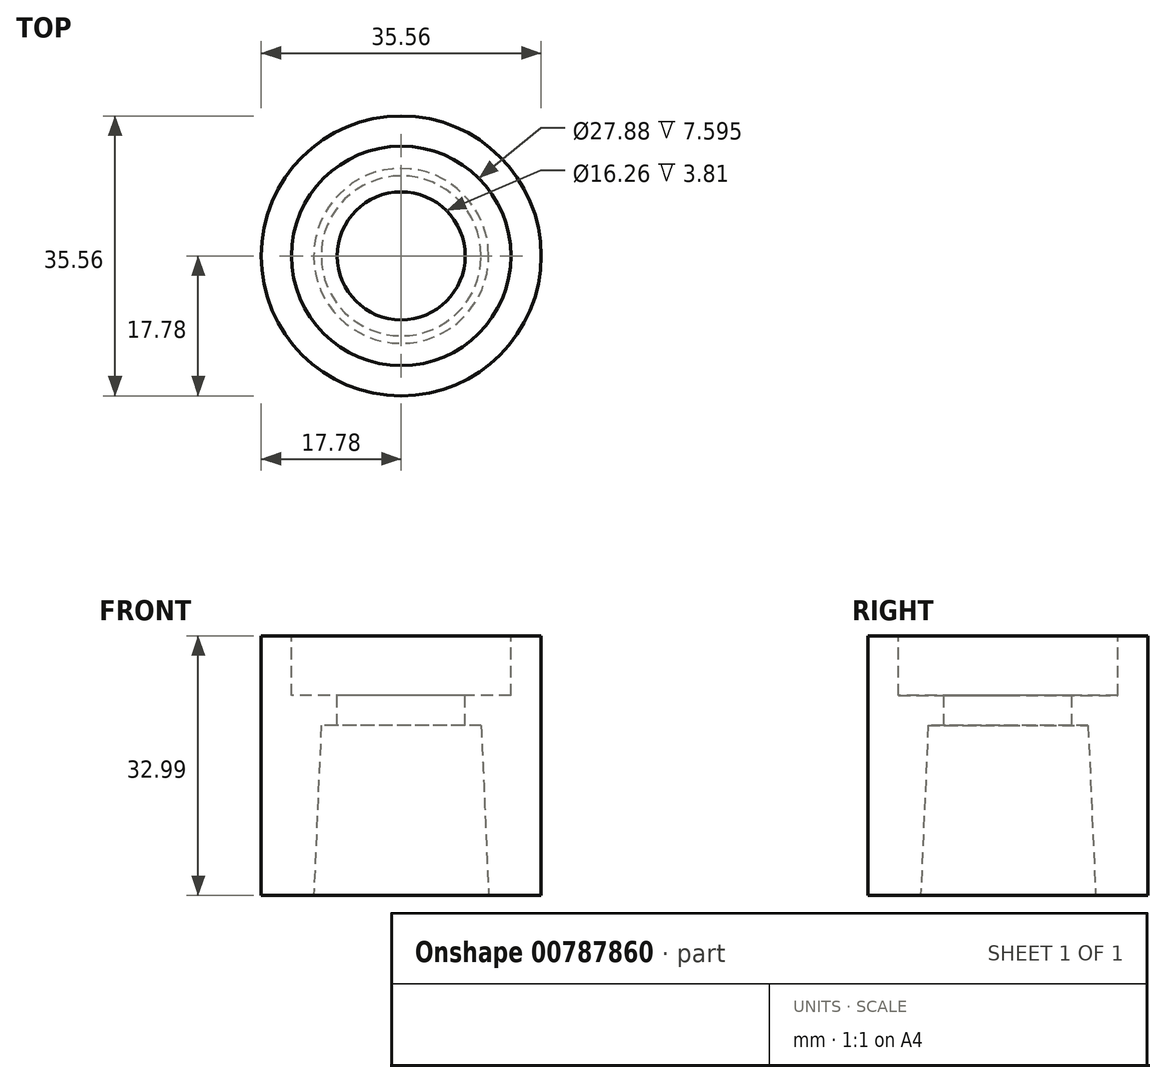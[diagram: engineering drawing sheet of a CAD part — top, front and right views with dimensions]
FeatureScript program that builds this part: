
annotation { "Feature Type Name" : "Feature", "Feature Type Description" : "" }
export const myFeature = defineFeature(function(context is Context, id is Id, definition is map)
    precondition{}
    {
        {
            var Q0;
            Q0=qCreatedBy(makeId("Front.planeOp"),FACE);
            var sketch = newSketch(context, id + "F0", { "sketchPlane" : qUnion([Q0])});
            skLineSegment(sketch, "E0", {"start": v(8.13, 25.4) * mm, "end": v(13.94, 25.4) * mm});
            skLineSegment(sketch, "E1", {"start": v(13.94, 25.4) * mm, "end": v(13.94, 33) * mm});
            skLineSegment(sketch, "E2", {"start": v(13.94, 33) * mm, "end": v(17.78, 33) * mm});
            skLineSegment(sketch, "E3", {"start": v(0, 21.59) * mm, "end": v(0, 0) * mm, "construction": true});
            skLineSegment(sketch, "E4", {"start": v(11.11, 0) * mm, "end": v(10.16, 21.59) * mm});
            skLineSegment(sketch, "E5", {"start": v(10.16, 21.59) * mm, "end": v(8.13, 21.59) * mm});
            skLineSegment(sketch, "E6", {"start": v(0, 21.59) * mm, "end": v(0, 25.4) * mm});
            skLineSegment(sketch, "E7", {"start": v(17.78, 33) * mm, "end": v(17.78, 0) * mm});
            skLineSegment(sketch, "E8", {"start": v(17.78, 0) * mm, "end": v(11.11, 0) * mm});
            skLineSegment(sketch, "E9", {"start": v(8.13, 25.4) * mm, "end": v(8.13, 21.59) * mm});
            skSolve(sketch);
        }
        {
            var Q0;
            Q0=makeQuery(id+"F0.imprint","IMPRINT",FACE,{"disambiguationData":[TD([[makeQuery(id+"F0.imprint","IMPRINT",EDGE,{"derivedFrom":sQuery(id+"F0.wireOp",EDGE,"E0")}),-1.0]])]});
            var Q1;
            Q1=sQuery(id+"F0.wireOp",EDGE,"E3");
            revolve(context, id + "F1", {"surfaceOperationType" : NewSurfaceOperationType.NEW, "entities" : qUnion([Q0]), "axis" : qUnion([Q1]), "revolveType" : RevolveType.FULL});
        }
    });
